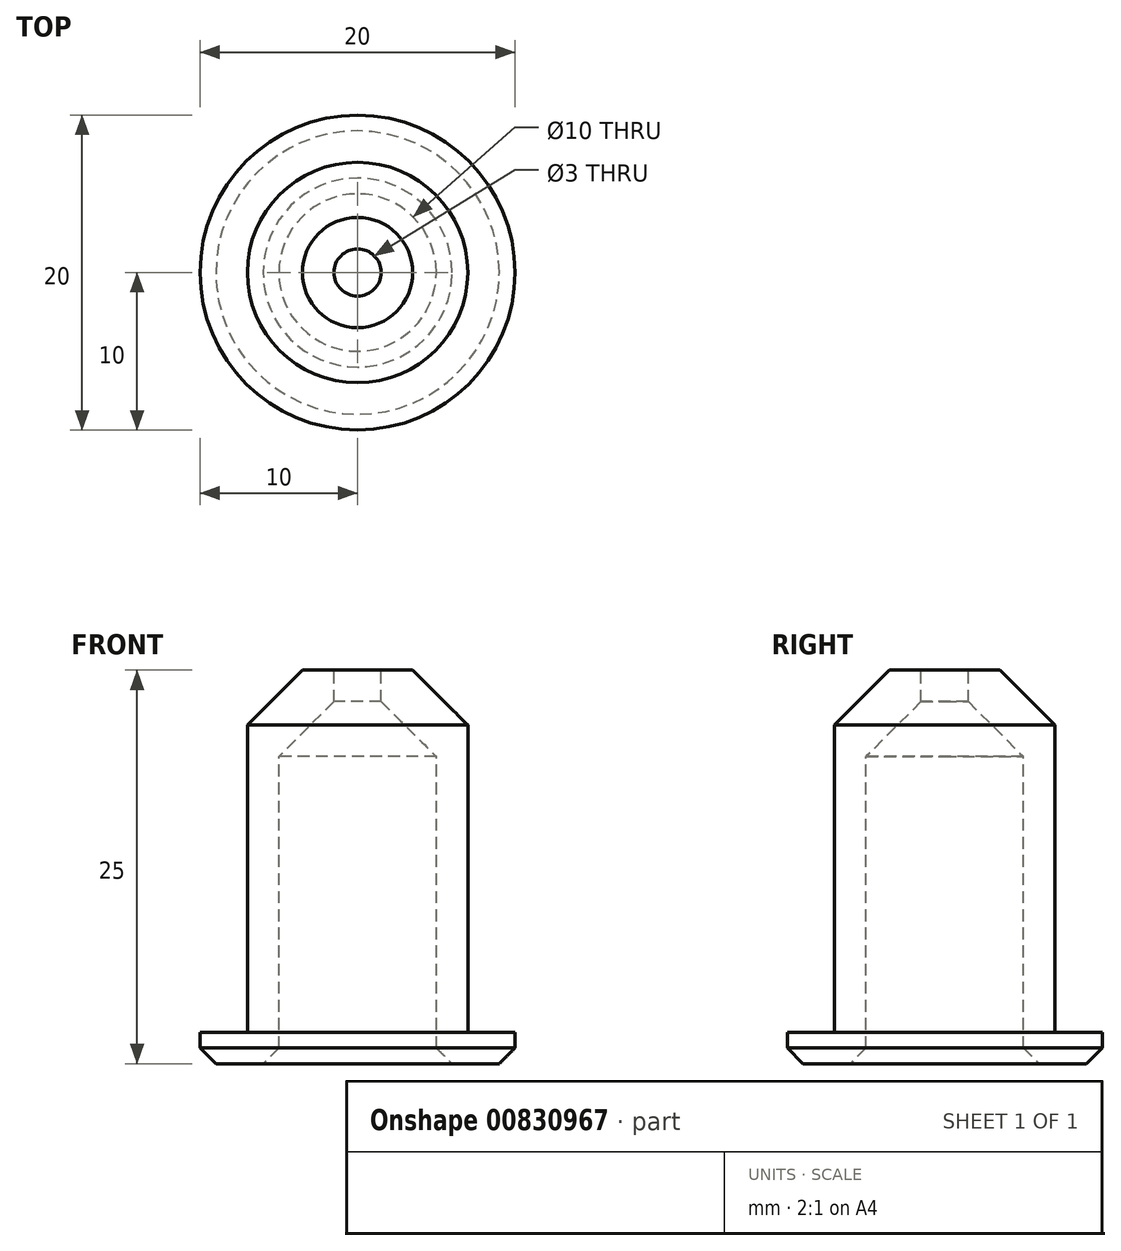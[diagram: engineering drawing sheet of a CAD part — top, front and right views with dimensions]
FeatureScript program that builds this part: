
annotation { "Feature Type Name" : "Feature", "Feature Type Description" : "" }
export const myFeature = defineFeature(function(context is Context, id is Id, definition is map)
    precondition{}
    {
        {
            var Q0;
            Q0=qCreatedBy(makeId("Top.planeOp"),FACE);
            var sketch = newSketch(context, id + "F0", { "sketchPlane" : qUnion([Q0])});
            skCircle(sketch, "E0", {"center": v(0, 0) * mm, "radius": 1.5 * mm});
            skCircle(sketch, "E1", {"center": v(0, 0) * mm, "radius": 7 * mm});
            skSolve(sketch);
        }
        {
            var Q0;
            Q0=makeQuery(id+"F0.imprint","IMPRINT",FACE,{"disambiguationData":[TD([[makeQuery(id+"F0.imprint","IMPRINT",EDGE,{"derivedFrom":sQuery(id+"F0.wireOp",EDGE,"E0")}),-1.0]])]});
            var Q1;
            Q1=makeQuery(id+"F0.imprint","IMPRINT",FACE,{"disambiguationData":[TD([[makeQuery(id+"F0.imprint","IMPRINT",EDGE,{"derivedFrom":sQuery(id+"F0.wireOp",EDGE,"E0")}),1.0]])]});
            extrude(context, id + "F1", {"entities" : qUnion([Q0, Q1]), "oppositeDirection" : true, "depth" : 25 * mm, "offsetDistance" : 25 * mm});
        }
        {
            var Q0;
            Q0=makeQuery(id+"F1.opExtrude","CAP_FACE",FACE,{"disambiguationData":[OSD([sQuery(id+"F0.wireOp",EDGE,"E1")])],"isStart":false});
            shell(context, id + "F2", {"entities" : qUnion([Q0]), "thickness" : 2 * mm});
        }
        {
            var Q0;
            Q0=makeQuery(id+"F0.imprint","IMPRINT",FACE,{"disambiguationData":[TD([[makeQuery(id+"F0.imprint","IMPRINT",EDGE,{"derivedFrom":sQuery(id+"F0.wireOp",EDGE,"E0")}),1.0]])]});
            extrude(context, id + "F3", {"entities" : qUnion([Q0]), "operationType" : NewBodyOperationType.REMOVE, "oppositeDirection" : true, "depth" : 25 * mm, "offsetDistance" : 25 * mm});
        }
        {
            var Q0;
            Q0=makeQuery(id+"F1.opExtrude","CAP_FACE",FACE,{"disambiguationData":[OSD([sQuery(id+"F0.wireOp",EDGE,"E1")])],"isStart":false});
            var sketch = newSketch(context, id + "F4", { "sketchPlane" : qUnion([Q0])});
            skCircle(sketch, "E2", {"center": v(0, 0) * mm, "radius": 10 * mm});
            skSolve(sketch);
        }
        {
            var Q0;
            Q0=makeQuery(id+"F4.imprint","IMPRINT",FACE,{"disambiguationData":[TD([[makeQuery(id+"F4.imprint","IMPRINT",EDGE,{"derivedFrom":sQuery(id+"F4.wireOp",EDGE,"E2")}),1.0]])]});
            extrude(context, id + "F5", {"entities" : qUnion([Q0]), "operationType" : NewBodyOperationType.ADD, "oppositeDirection" : true, "depth" : 2 * mm, "offsetDistance" : 25 * mm});
        }
        {
            var Q0;
            Q0=makeQuery(id+"F5.opExtrude","CAP_EDGE",EDGE,{"disambiguationData":[OSD([sQuery(id+"F0.wireOp",EDGE,"E1")])],"isStart":false});
            var Q1;
            {var subQ0=sQuery(id+"F0.wireOp",EDGE,"E1");Q1=makeQuery(id+"F2.opShell","OFFSET_EDGE",EDGE,{"disambiguationData":[OSD([subQ0]),TDD([makeQuery(id+"F1.opExtrude","CAP_EDGE",EDGE,{"disambiguationData":[OSD([subQ0])],"isStart":false})])]});}
            var Q2;
            Q2=makeQuery(id+"F5.opExtrude","CAP_EDGE",EDGE,{"disambiguationData":[OSD([sQuery(id+"F4.wireOp",EDGE,"E2")])],"isStart":true});
            chamfer(context, id + "F6", {"entities" : qUnion([Q0, Q1, Q2]), "width" : 1 * mm, "tangentPropagation" : true});
        }
        {
            var Q0;
            Q0=makeQuery(id+"F1.opExtrude","CAP_EDGE",EDGE,{"disambiguationData":[OSD([sQuery(id+"F0.wireOp",EDGE,"E1")])],"isStart":true});
            var Q1;
            {var subQ0=sQuery(id+"F0.wireOp",EDGE,"E1");Q1=makeQuery(id+"F2.opShell","OFFSET_EDGE",EDGE,{"disambiguationData":[OSD([subQ0]),TDD([makeQuery(id+"F1.opExtrude","CAP_EDGE",EDGE,{"disambiguationData":[OSD([subQ0])],"isStart":true})])]});}
            chamfer(context, id + "F7", {"entities" : qUnion([Q0, Q1]), "width" : 3.5 * mm, "tangentPropagation" : true});
        }
    });
